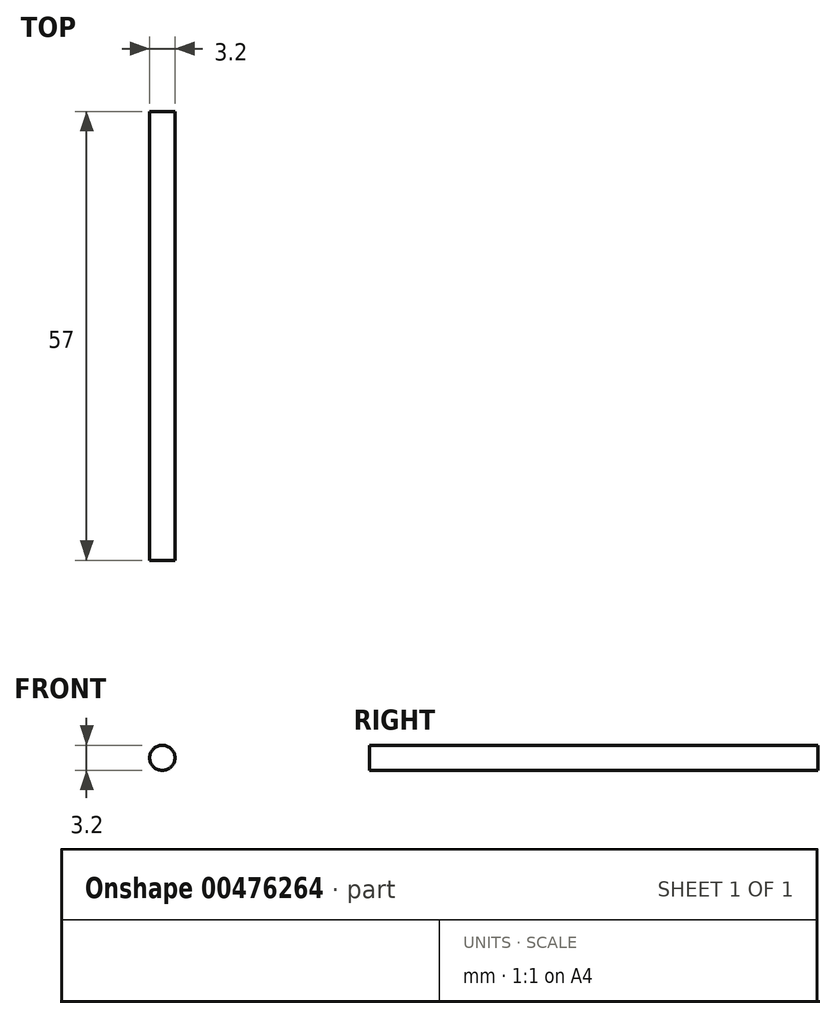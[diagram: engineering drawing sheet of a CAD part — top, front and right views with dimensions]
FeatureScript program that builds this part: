
annotation { "Feature Type Name" : "Feature", "Feature Type Description" : "" }
export const myFeature = defineFeature(function(context is Context, id is Id, definition is map)
    precondition{}
    {
        {
            var Q0;
            Q0=qCreatedBy(makeId("Front.planeOp"),FACE);
            var sketch = newSketch(context, id + "F0", { "sketchPlane" : qUnion([Q0])});
            skCircle(sketch, "E0", {"center": v(-40.13, 33.23) * mm, "radius": 1.6 * mm});
            skPoint(sketch, "E0.first.point", {"position": v(-41.58, 33.9) * mm});
            skPoint(sketch, "E0.second.point", {"position": v(-38.94, 32.16) * mm});
            skPoint(sketch, "E0.third.point", {"position": v(-41.32, 32.16) * mm});
            skSolve(sketch);
        }
        {
            var Q0;
            Q0=makeQuery(id+"F0.imprint","IMPRINT",FACE,{"disambiguationData":[TD([[makeQuery(id+"F0.imprint","IMPRINT",EDGE,{"derivedFrom":sQuery(id+"F0.wireOp",EDGE,"E0")}),1.0]])]});
            extrude(context, id + "F1", {"entities" : qUnion([Q0]), "depth" : 57 * mm});
        }
    });
